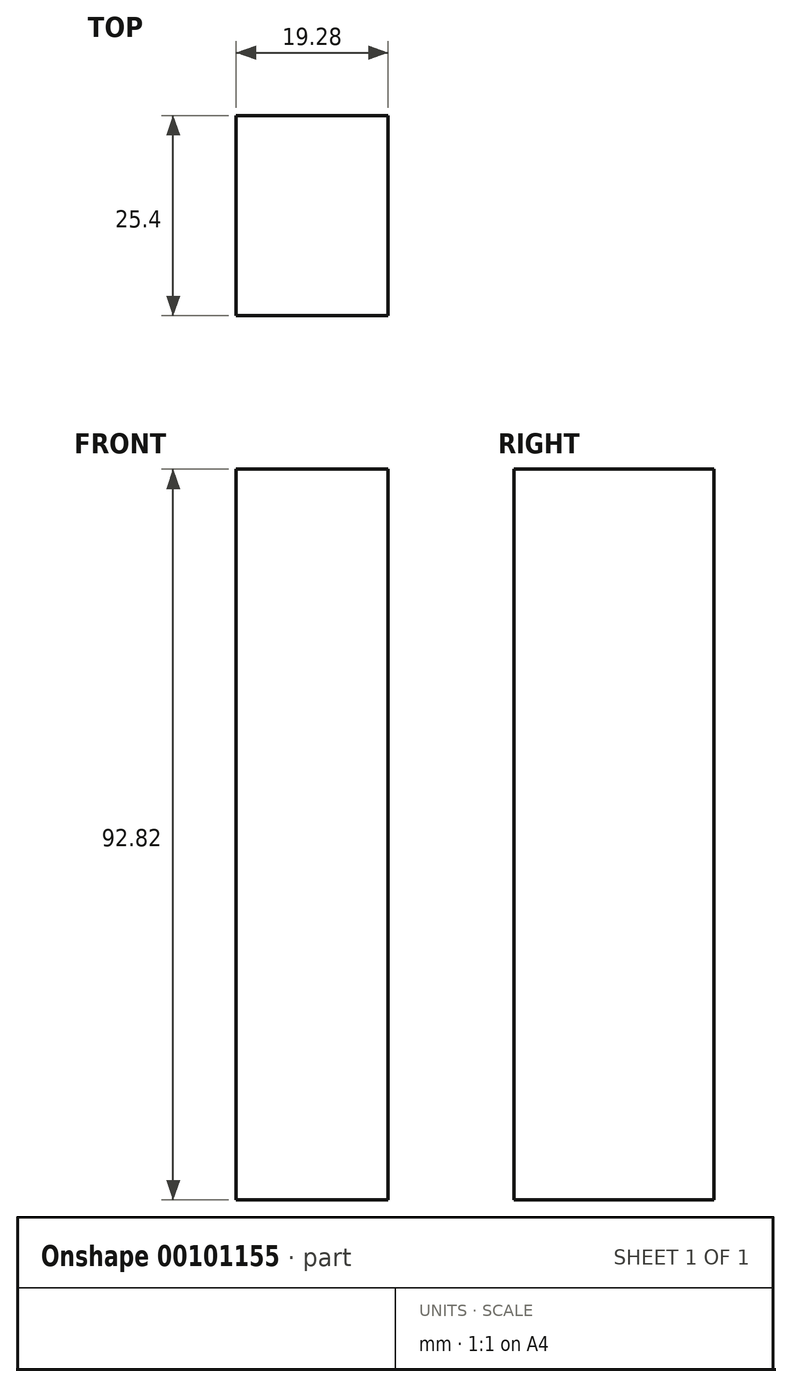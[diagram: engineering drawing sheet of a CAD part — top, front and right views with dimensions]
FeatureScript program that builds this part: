
annotation { "Feature Type Name" : "Feature", "Feature Type Description" : "" }
export const myFeature = defineFeature(function(context is Context, id is Id, definition is map)
    precondition{}
    {
        {
            var Q0;
            Q0=qCreatedBy(makeId("Front.planeOp"),FACE);
            var sketch = newSketch(context, id + "F0", { "sketchPlane" : qUnion([Q0])});
            skLineSegment(sketch, "E0.bottom", {"start": v(9.64, -46.41) * mm, "end": v(-9.64, -46.41) * mm});
            skLineSegment(sketch, "E0.top", {"start": v(9.64, 46.41) * mm, "end": v(-9.64, 46.41) * mm});
            skLineSegment(sketch, "E0.left", {"start": v(9.64, -46.41) * mm, "end": v(9.64, 46.41) * mm});
            skLineSegment(sketch, "E0.right", {"start": v(-9.64, -46.41) * mm, "end": v(-9.64, 46.41) * mm});
            skPoint(sketch, "E0.middle", {"position": v(0, 0) * mm});
            skSolve(sketch);
        }
        {
            var Q0;
            Q0=makeQuery(id+"F0.imprint","IMPRINT",FACE,{"disambiguationData":[TD([[makeQuery(id+"F0.imprint","IMPRINT",EDGE,{"derivedFrom":sQuery(id+"F0.wireOp",EDGE,"E0.bottom")}),-1.0]])]});
            extrude(context, id + "F1", {"entities" : qUnion([Q0]), "depth" : 25.4 * mm});
        }
    });
